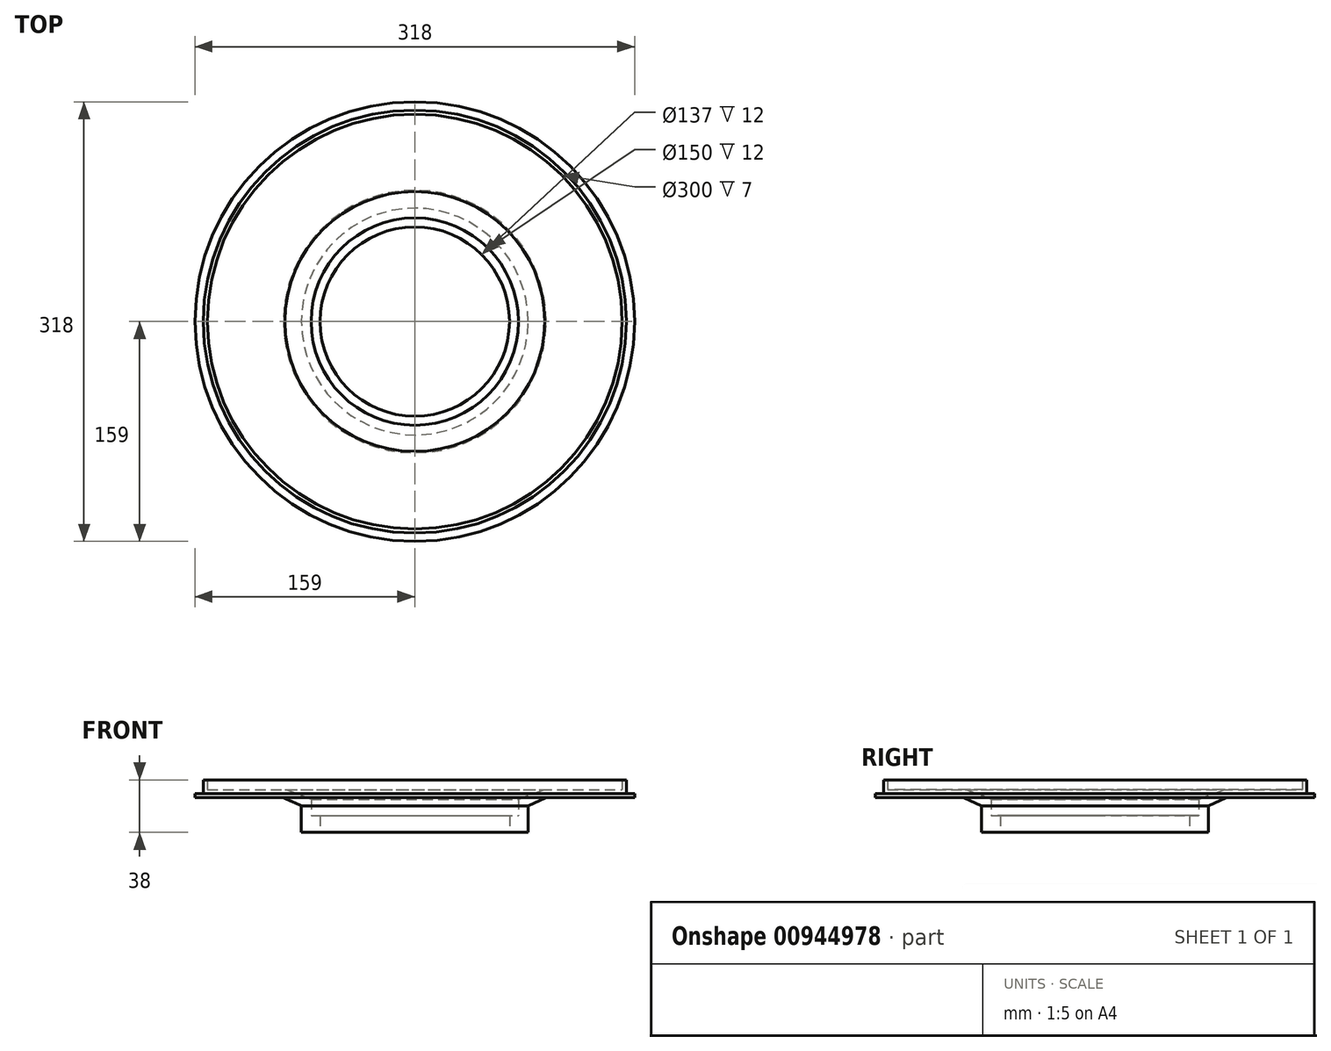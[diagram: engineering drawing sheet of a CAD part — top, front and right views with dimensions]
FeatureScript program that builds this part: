
annotation { "Feature Type Name" : "Feature", "Feature Type Description" : "" }
export const myFeature = defineFeature(function(context is Context, id is Id, definition is map)
    precondition{}
    {
        {
            var Q0;
            Q0=qCreatedBy(makeId("Front.planeOp"),FACE);
            var sketch = newSketch(context, id + "F0", { "sketchPlane" : qUnion([Q0])});
            skLineSegment(sketch, "E0", {"start": v(-68.5, 0) * mm, "end": v(-68.5, 12) * mm});
            skLineSegment(sketch, "E1", {"start": v(-68.5, 12) * mm, "end": v(-75, 12) * mm});
            skLineSegment(sketch, "E2", {"start": v(-75, 12) * mm, "end": v(-75, 24) * mm});
            skLineSegment(sketch, "E3", {"start": v(-75, 24) * mm, "end": v(-94, 31) * mm});
            skLineSegment(sketch, "E4", {"start": v(-95, 25) * mm, "end": v(-82, 19.21) * mm});
            skLineSegment(sketch, "E5", {"start": v(-82, 19.21) * mm, "end": v(-82, 0) * mm});
            skLineSegment(sketch, "E6", {"start": v(-82, 0) * mm, "end": v(-68.5, 0) * mm});
            skLineSegment(sketch, "E7", {"start": v(-95, 25) * mm, "end": v(-159, 25) * mm});
            skLineSegment(sketch, "E8", {"start": v(-159, 25) * mm, "end": v(-159, 28) * mm});
            skLineSegment(sketch, "E9", {"start": v(-159, 28) * mm, "end": v(-153, 28) * mm});
            skLineSegment(sketch, "E10", {"start": v(-153, 28) * mm, "end": v(-153, 38) * mm});
            skLineSegment(sketch, "E11", {"start": v(-153, 38) * mm, "end": v(-150, 38) * mm});
            skLineSegment(sketch, "E12", {"start": v(-150, 38) * mm, "end": v(-150, 31) * mm});
            skLineSegment(sketch, "E13", {"start": v(-150, 31) * mm, "end": v(-94, 31) * mm});
            skSolve(sketch);
        }
        {
            var Q0;
            Q0=qCreatedBy(makeId("Top.planeOp"),FACE);
            var sketch = newSketch(context, id + "F1", { "sketchPlane" : qUnion([Q0])});
            skCircle(sketch, "E14", {"center": v(0, 0) * mm, "radius": 68.5 * mm, "construction": true});
            skSolve(sketch);
        }
        {
            var Q0;
            Q0=makeQuery(id+"F0.imprint","IMPRINT",FACE,{"disambiguationData":[TD([[makeQuery(id+"F0.imprint","IMPRINT",EDGE,{"derivedFrom":sQuery(id+"F0.wireOp",EDGE,"E0")}),1.0]])]});
            var Q1;
            Q1=sQuery(id+"F1.wireOp",EDGE,"E14");
            revolve(context, id + "F2", {"surfaceOperationType" : NewSurfaceOperationType.NEW, "entities" : qUnion([Q0]), "axis" : qUnion([Q1]), "revolveType" : RevolveType.FULL});
        }
    });
